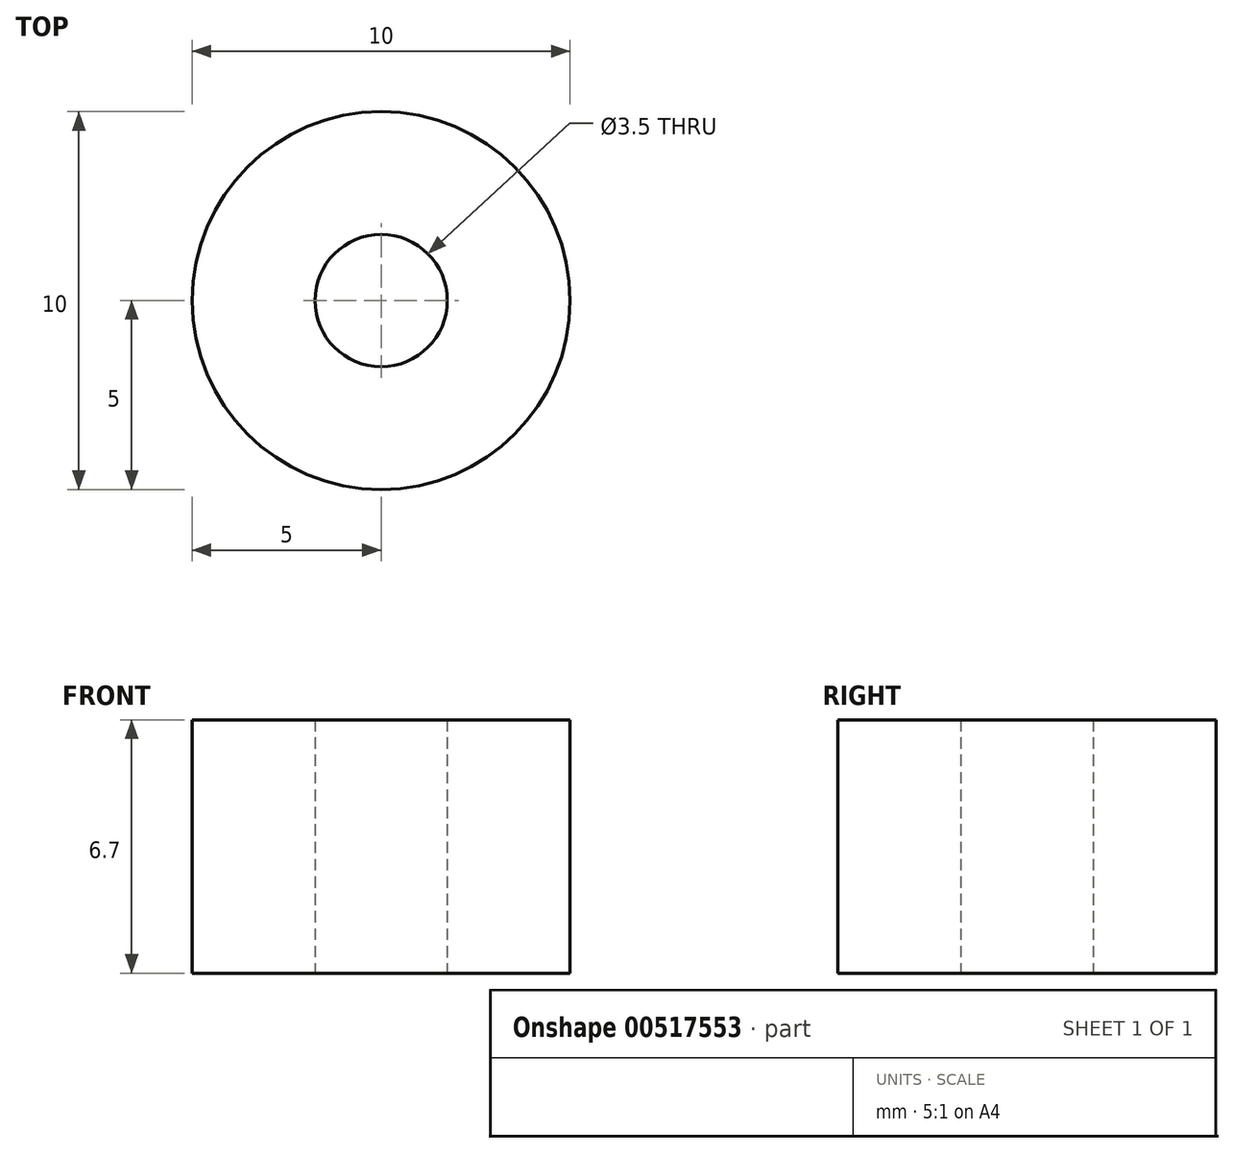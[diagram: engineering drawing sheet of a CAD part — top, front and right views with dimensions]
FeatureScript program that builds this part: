
annotation { "Feature Type Name" : "Feature", "Feature Type Description" : "" }
export const myFeature = defineFeature(function(context is Context, id is Id, definition is map)
    precondition{}
    {
        {
            var Q0;
            Q0=qCreatedBy(makeId("Top.planeOp"),FACE);
            var sketch = newSketch(context, id + "F0", { "sketchPlane" : qUnion([Q0])});
            skCircle(sketch, "E0", {"center": v(0, 0) * mm, "radius": 1.75 * mm});
            skCircle(sketch, "E1", {"center": v(0, 0) * mm, "radius": 5 * mm});
            skSolve(sketch);
        }
        {
            var Q0;
            Q0 = qSketchRegion(id + "F0", true);
            extrude(context, id + "F1", {"entities" : qUnion([Q0]), "depth" : 6.7 * mm, "offsetDistance" : 25 * mm});
        }
    });
